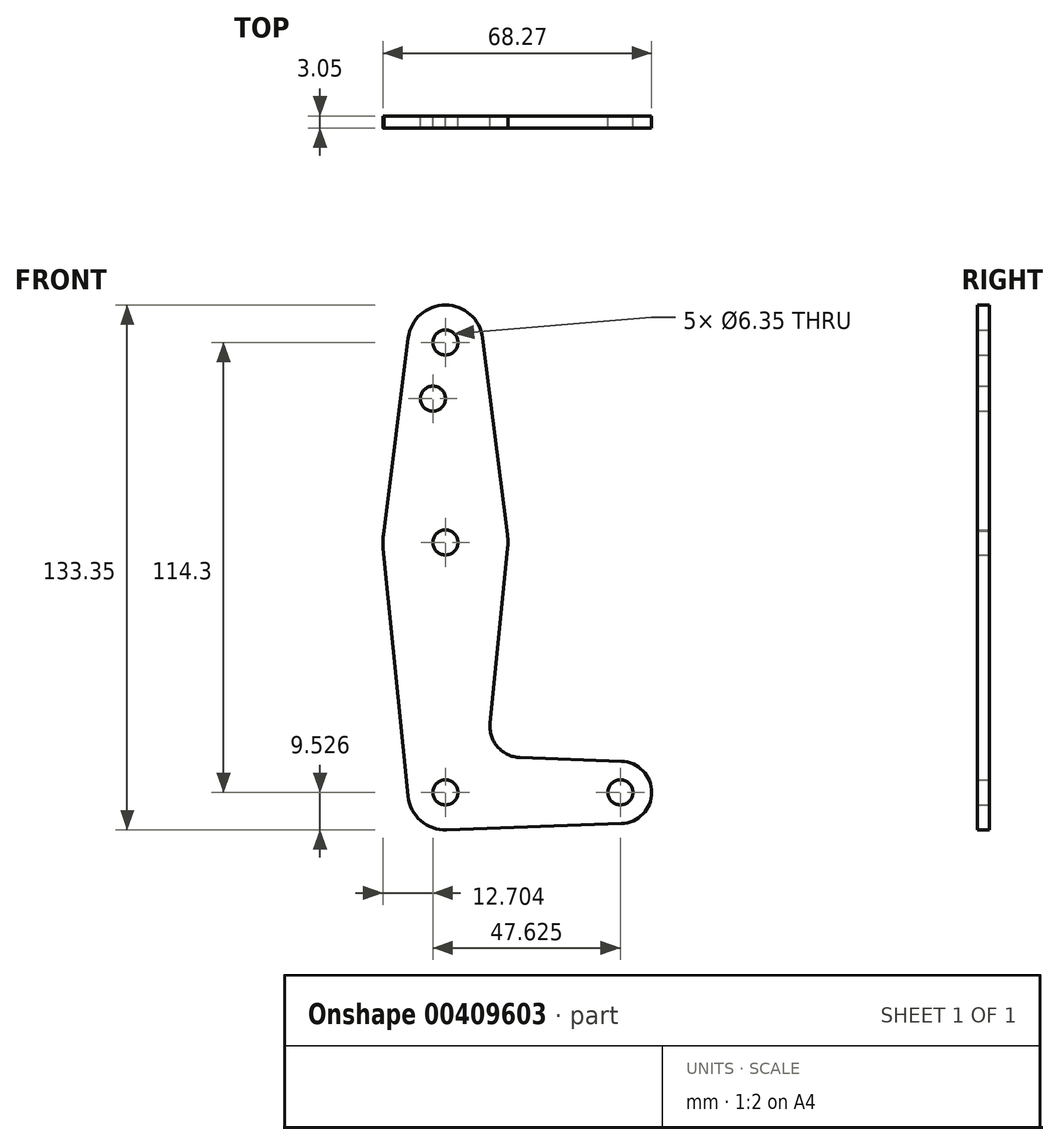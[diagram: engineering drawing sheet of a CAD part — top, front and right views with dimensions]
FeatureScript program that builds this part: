
annotation { "Feature Type Name" : "Feature", "Feature Type Description" : "" }
export const myFeature = defineFeature(function(context is Context, id is Id, definition is map)
    precondition{}
    {
        {
            var Q0;
            Q0=qCreatedBy(makeId("Front.planeOp"),FACE);
            var sketch = newSketch(context, id + "F0", { "sketchPlane" : qUnion([Q0])});
            skLineSegment(sketch, "E0", {"start": v(-37.04, 59.52) * mm, "end": v(-37.04, -54.78) * mm, "construction": true});
            skLineSegment(sketch, "E1", {"start": v(-37.04, -54.78) * mm, "end": v(7.4, -54.78) * mm, "construction": true});
            skCircle(sketch, "E2", {"center": v(-37.04, 59.52) * mm, "radius": 9.53 * mm});
            skCircle(sketch, "E3", {"center": v(-37.04, 8.72) * mm, "radius": 15.88 * mm});
            skCircle(sketch, "E4", {"center": v(-37.04, -54.78) * mm, "radius": 9.53 * mm});
            skCircle(sketch, "E5", {"center": v(7.4, -54.78) * mm, "radius": 7.94 * mm});
            skCircle(sketch, "E6", {"center": v(-40.22, 45.24) * mm, "radius": 3.18 * mm});
            skCircle(sketch, "E7", {"center": v(-37.04, 59.52) * mm, "radius": 3.18 * mm});
            skCircle(sketch, "E8", {"center": v(-37.04, 8.72) * mm, "radius": 3.18 * mm});
            skCircle(sketch, "E9", {"center": v(-37.04, -54.78) * mm, "radius": 3.18 * mm});
            skCircle(sketch, "E10", {"center": v(7.4, -54.78) * mm, "radius": 3.18 * mm});
            skPoint(sketch, "E11.orphan", {"position": v(-53.03, 8.72) * mm});
            skPoint(sketch, "E12.orphan", {"position": v(-21.05, 8.72) * mm});
            skPoint(sketch, "E13.start.orphan", {"position": v(-46.63, 59.52) * mm});
            skPoint(sketch, "E14.start.orphan", {"position": v(-27.45, 59.52) * mm});
            skPoint(sketch, "E15.end.orphan", {"position": v(-46.61, -54.78) * mm});
            skLineSegment(sketch, "E16", {"start": v(-46.5, 60.7) * mm, "end": v(-52.63, 11.7) * mm});
            skLineSegment(sketch, "E17", {"start": v(-27.6, 60.7) * mm, "end": v(-21.3, 10.7) * mm});
            skLineSegment(sketch, "E18", {"start": v(-52.84, 7.13) * mm, "end": v(-46.52, -55.74) * mm});
            skLineSegment(sketch, "E19", {"start": v(-36.7, -64.3) * mm, "end": v(7.7, -62.72) * mm});
            skLineSegment(sketch, "E20", {"start": v(-18.07, -45.93) * mm, "end": v(7.7, -46.85) * mm});
            skLineSegment(sketch, "E21", {"start": v(-21.25, 7.13) * mm, "end": v(-25.7, -37.2) * mm});
            skArc(sketch, "E22.filletArc", {"start": v(-25.7, -37.2) * mm, "mid": v(-23.78, -43.21) * mm, "end": v(-18.07, -45.93) * mm});
            skSolve(sketch);
        }
        {
            var Q0;
            Q0=makeQuery(id+"F0.imprint","IMPRINT",FACE,{"disambiguationData":[TD([[makeQuery(id+"F0.imprint","IMPRINT",EDGE,{"derivedFrom":sQuery(id+"F0.wireOp",EDGE,"E7")}),-1.0]])]});
            var Q1;
            Q1=makeQuery(id+"F0.imprint","IMPRINT",FACE,{"disambiguationData":[TD([[makeQuery(id+"F0.imprint","IMPRINT",EDGE,{"derivedFrom":sQuery(id+"F0.wireOp",EDGE,"E6")}),-1.0]])]});
            var Q2;
            {var subQ3=sQuery(id+"F0.wireOp",EDGE,"E18");Q2=makeQuery(id+"F0.imprint","IMPRINT",FACE,{"disambiguationData":[TD([[makeQuery(id+"F0.imprint","IMPRINT",EDGE,{"derivedFrom":subQ3}),1.0]])]});}
            var Q3;
            Q3=makeQuery(id+"F0.imprint","IMPRINT",FACE,{"disambiguationData":[TD([[makeQuery(id+"F0.imprint","IMPRINT",EDGE,{"derivedFrom":sQuery(id+"F0.wireOp",EDGE,"E8")}),-1.0]])]});
            var Q4;
            Q4=makeQuery(id+"F0.imprint","IMPRINT",FACE,{"disambiguationData":[TD([[makeQuery(id+"F0.imprint","IMPRINT",EDGE,{"derivedFrom":sQuery(id+"F0.wireOp",EDGE,"E9")}),-1.0]])]});
            var Q5;
            Q5=makeQuery(id+"F0.imprint","IMPRINT",FACE,{"disambiguationData":[TD([[makeQuery(id+"F0.imprint","IMPRINT",EDGE,{"derivedFrom":sQuery(id+"F0.wireOp",EDGE,"E10")}),-1.0]])]});
            extrude(context, id + "F1", {"entities" : qUnion([Q0, Q1, Q2, Q3, Q4, Q5]), "depth" : 3.05 * mm});
        }
    });
